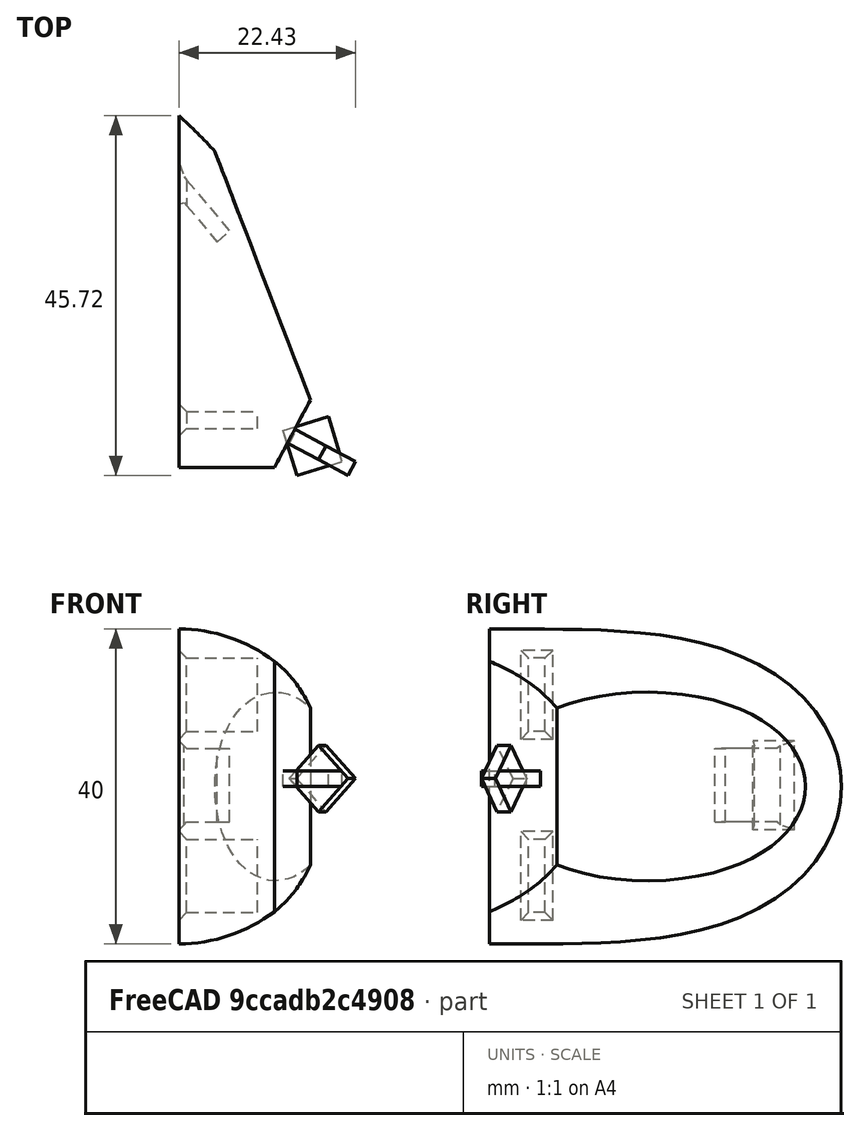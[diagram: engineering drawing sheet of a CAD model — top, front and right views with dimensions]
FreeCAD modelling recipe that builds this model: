
FCSTD DOCUMENT  (FreeCAD 0.14R3702 (Git))
Label: bicho_base
License: CC-BY 3.0
LicenseURL: http://creativecommons.org/licenses/by/3.0/
objects: Part::Box×8, Part::Cut×4, Part::Torus×1, Part::MultiFuse×1, Part::Chamfer×1
note: 15 computed .brp shape members not serialized (recipe doc carries the construction recipe); baked Part::Feature solids carry a one-line shape summary decoded from their .brp

FEATURE [Part::Torus] Torus
  Angle1 = -180
  Angle2 = 180
  Angle3 = 50
  Radius1 = 40
  Radius2 = 20
FEATURE [Part::Box] Box  label="Cube"
  Height = 68
  Length = 30
  Placement = pos=(10,-1,-38) rot=(0,0,1;0rad)
  Width = 66
FEATURE [Part::Cut] Cut  label="base"
  Base = -> Torus
  Tool = -> Box
FEATURE [Part::Box] Box001  label="Cube001"
  Height = 52
  Length = 7
  Placement = pos=(60,0,-25) rot=(0,0,1;0.366519rad)
  Width = 44
FEATURE [Part::Cut] Cut001  label="base-espalda"
  Base = -> Cut
  Tool = -> Box001
FEATURE [Part::Box] Box002  label="pata"
  Height = 9.3
  Length = 20
  Placement = pos=(30,5,-16) rot=(0,0,1;0rad)
  Width = 2.1
FEATURE [Part::Box] Box003  label="pata001"
  Height = 9.3
  Length = 20
  Placement = pos=(32,44,-4.5) rot=(0,0,-1;0.872665rad)
  Width = 2.1
FEATURE [Part::Box] Box004  label="pata002"
  Height = 9.3
  Length = 20
  Placement = pos=(30,5,7) rot=(0,0,1;0rad)
  Width = 2.1
FEATURE [Part::MultiFuse] Fusion  label="patas"
  Shapes = -> [Box002,Box003,Box004]
FEATURE [Part::Cut] Cut002  label="bicho"
  Base = -> Cut001
  Tool = -> Fusion
FEATURE [Part::Chamfer] Chamfer
  Base = -> Cut002
  Edges = 12 edges r=1: [Edge8,Edge9,Edge10,Edge11,Edge12,Edge13,Edge14,Edge15,Edge16,Edge17,Edge18,Edge19]
FEATURE [Part::Box] Box005  label="Cubo"
  Height = 40
  Length = 10
  Placement = pos=(50,-4,-21) rot=(0,0,-1;0.488692rad)
  Width = 20
FEATURE [Part::Cut] Cut003  label="base_3_plamos"
  Base = -> Chamfer
  Tool = -> Box005
FEATURE [Part::Box] Box006  label="Cubo001"
  Height = 6
  Length = 6
  Placement = pos=(54,3,1) rot=(0.208902,0.837859,-0.504333;0.918268rad)
  Width = 2
FEATURE [Part::Box] Box007  label="Cubo002"
  Height = 2
  Length = 6
  Placement = pos=(55,-1,0) rot=(0,0,1;0.296706rad)
  Width = 6
